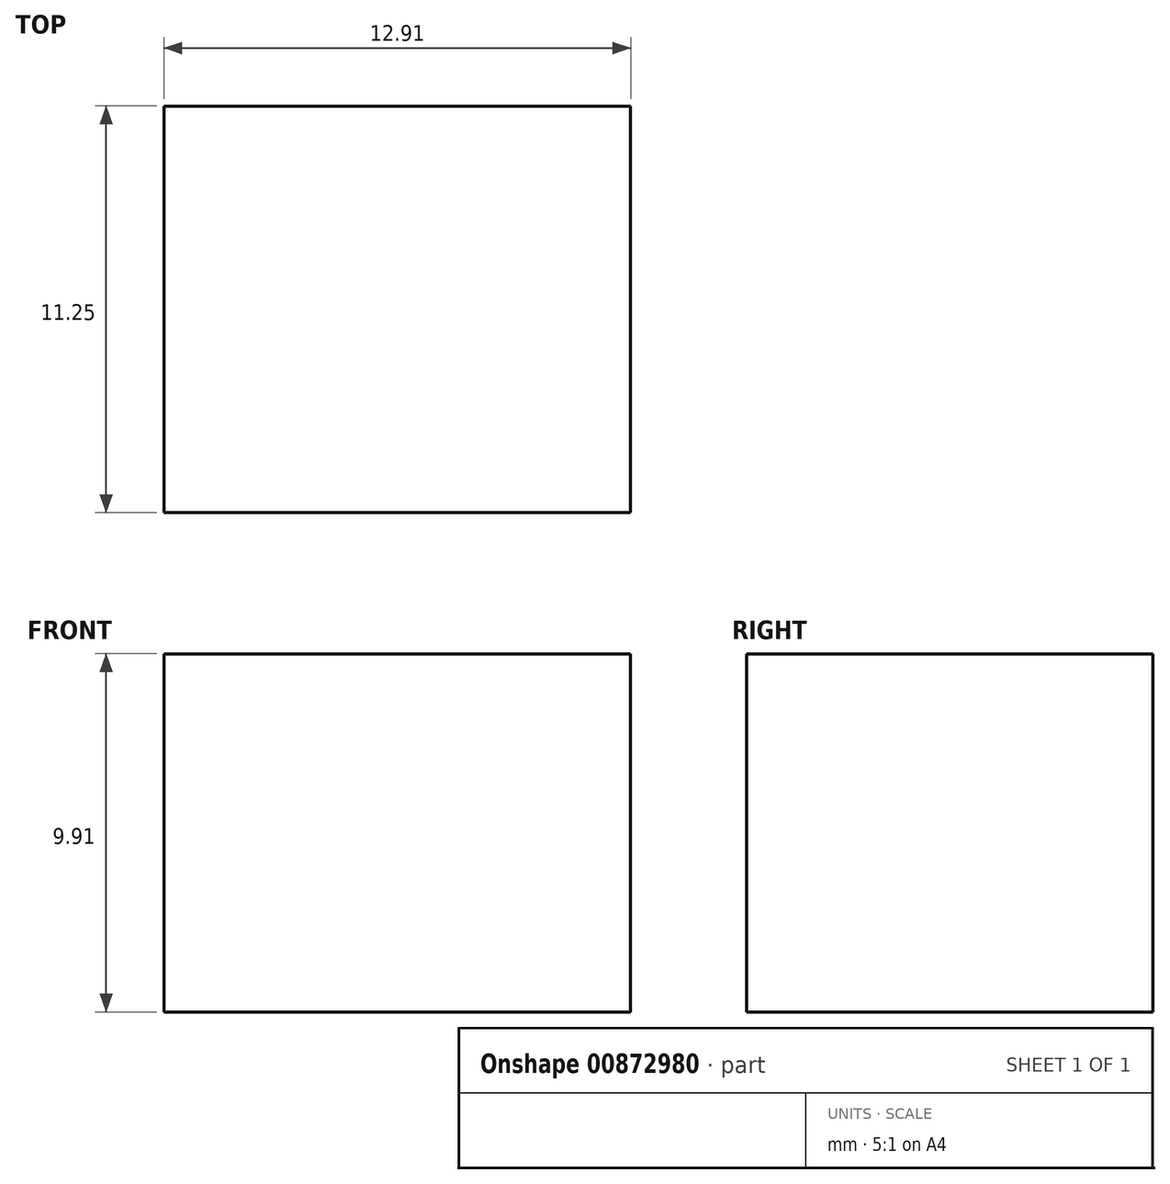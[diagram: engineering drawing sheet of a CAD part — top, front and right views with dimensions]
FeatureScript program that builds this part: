
annotation { "Feature Type Name" : "Feature", "Feature Type Description" : "" }
export const myFeature = defineFeature(function(context is Context, id is Id, definition is map)
    precondition{}
    {
        {
            var Q0;
            Q0=qCreatedBy(makeId("Top.planeOp"),FACE);
            var sketch = newSketch(context, id + "F0", { "sketchPlane" : qUnion([Q0])});
            skLineSegment(sketch, "E0.bottom", {"start": v(-6.73, 5.44) * mm, "end": v(6.18, 5.44) * mm});
            skLineSegment(sketch, "E0.top", {"start": v(-6.73, -5.8) * mm, "end": v(6.18, -5.8) * mm});
            skLineSegment(sketch, "E0.left", {"start": v(-6.73, 5.44) * mm, "end": v(-6.73, -5.8) * mm});
            skLineSegment(sketch, "E0.right", {"start": v(6.18, 5.44) * mm, "end": v(6.18, -5.8) * mm});
            skSolve(sketch);
        }
        {
            var Q0;
            Q0 = qSketchRegion(id + "F0", true);
            extrude(context, id + "F1", {"entities" : qUnion([Q0]), "depth" : 9.9 * mm, "offsetDistance" : 25.4 * mm});
        }
    });
